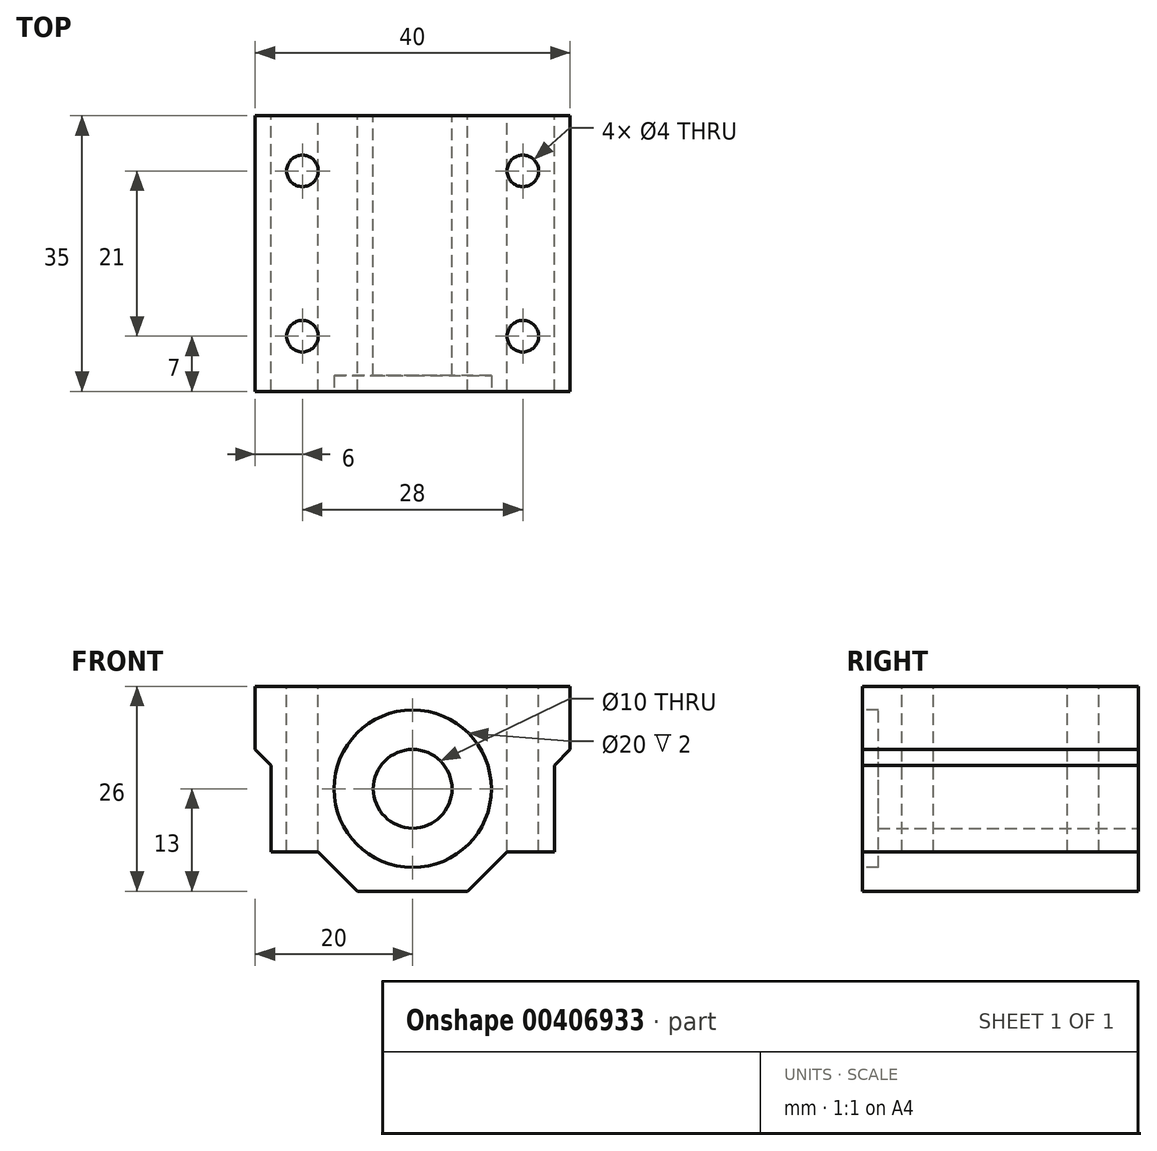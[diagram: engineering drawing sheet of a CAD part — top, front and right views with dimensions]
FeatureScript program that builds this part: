
annotation { "Feature Type Name" : "Feature", "Feature Type Description" : "" }
export const myFeature = defineFeature(function(context is Context, id is Id, definition is map)
    precondition{}
    {
        {
            var Q0;
            Q0=qCreatedBy(makeId("Front.planeOp"),FACE);
            var sketch = newSketch(context, id + "F0", { "sketchPlane" : qUnion([Q0])});
            skCircle(sketch, "E0", {"center": v(0, 0) * mm, "radius": 5 * mm});
            skLineSegment(sketch, "E1", {"start": v(-42.65, 13) * mm, "end": v(49.52, 13) * mm, "construction": true});
            skLineSegment(sketch, "E2", {"start": v(0, 13) * mm, "end": v(-20, 13) * mm});
            skLineSegment(sketch, "E3", {"start": v(-20, 13) * mm, "end": v(-20, 5) * mm});
            skLineSegment(sketch, "E4", {"start": v(-20, 5) * mm, "end": v(-18, 3) * mm});
            skLineSegment(sketch, "E5", {"start": v(-18, 3) * mm, "end": v(-18, -8) * mm});
            skLineSegment(sketch, "E6", {"start": v(-18, -8) * mm, "end": v(-12, -8) * mm});
            skLineSegment(sketch, "E7", {"start": v(-12, -8) * mm, "end": v(-7, -13) * mm});
            skLineSegment(sketch, "E8", {"start": v(-7, -13) * mm, "end": v(0, -13) * mm});
            skCircle(sketch, "E9", {"center": v(0, 0) * mm, "radius": 10 * mm, "construction": true});
            skLineSegment(sketch, "E10.MirrorCS", {"start": v(20, 13) * mm, "end": v(20, 5) * mm});
            skLineSegment(sketch, "E11.MirrorCS", {"start": v(20, 5) * mm, "end": v(18, 3) * mm});
            skLineSegment(sketch, "E12.MirrorCS", {"start": v(18, 3) * mm, "end": v(18, -8) * mm});
            skLineSegment(sketch, "E13.MirrorCS", {"start": v(18, -8) * mm, "end": v(12, -8) * mm});
            skLineSegment(sketch, "E14.MirrorCS", {"start": v(12, -8) * mm, "end": v(7, -13) * mm});
            skLineSegment(sketch, "E15.MirrorCS", {"start": v(7, -13) * mm, "end": v(0, -13) * mm});
            skLineSegment(sketch, "E16.MirrorCS", {"start": v(42.65, 13) * mm, "end": v(-49.52, 13) * mm, "construction": true});
            skLineSegment(sketch, "E17", {"start": v(0, 13) * mm, "end": v(20, 13) * mm});
            skSolve(sketch);
        }
        {
            var Q0;
            Q0 = qSketchRegion(id + "F0", true);
            extrude(context, id + "F1", {"entities" : qUnion([Q0]), "endBound" : BoundingType.SYMMETRIC, "depth" : 35 * mm});
        }
        {
            var Q0;
            Q0=makeQuery(id+"F1.opExtrude","CAP_FACE",FACE,{"disambiguationData":[OSD([sQuery(id+"F0.wireOp",EDGE,"E0"),sQuery(id+"F0.wireOp",EDGE,"E2"),sQuery(id+"F0.wireOp",EDGE,"E3"),sQuery(id+"F0.wireOp",EDGE,"E4"),sQuery(id+"F0.wireOp",EDGE,"E5"),sQuery(id+"F0.wireOp",EDGE,"E6"),sQuery(id+"F0.wireOp",EDGE,"E7"),sQuery(id+"F0.wireOp",EDGE,"E8"),sQuery(id+"F0.wireOp",EDGE,"E10.MirrorCS"),sQuery(id+"F0.wireOp",EDGE,"E11.MirrorCS"),sQuery(id+"F0.wireOp",EDGE,"E12.MirrorCS"),sQuery(id+"F0.wireOp",EDGE,"E13.MirrorCS"),sQuery(id+"F0.wireOp",EDGE,"E14.MirrorCS"),sQuery(id+"F0.wireOp",EDGE,"E15.MirrorCS"),sQuery(id+"F0.wireOp",EDGE,"E17")])],"isStart":false});
            var sketch = newSketch(context, id + "F2", { "sketchPlane" : qUnion([Q0])});
            skCircle(sketch, "E18", {"center": v(0, 0) * mm, "radius": 10 * mm});
            skSolve(sketch);
        }
        {
            var Q0;
            Q0 = qSketchRegion(id + "F2", true);
            extrude(context, id + "F3", {"entities" : qUnion([Q0]), "operationType" : NewBodyOperationType.REMOVE, "oppositeDirection" : true, "depth" : 2 * mm});
        }
        {
            var Q0;
            Q0=makeQuery(id+"F1.opExtrude","SWEPT_FACE",FACE,{"disambiguationData":[OSD([sQuery(id+"F0.wireOp",EDGE,"E2"),sQuery(id+"F0.wireOp",EDGE,"E17")])]});
            var sketch = newSketch(context, id + "F4", { "sketchPlane" : qUnion([Q0])});
            skLineSegment(sketch, "E19", {"start": v(-14, -17.5) * mm, "end": v(-14, 17.5) * mm, "construction": true});
            skCircle(sketch, "E20", {"center": v(-14, 10.5) * mm, "radius": 2 * mm});
            skCircle(sketch, "E21.MirrorC", {"center": v(-14, -10.5) * mm, "radius": 2 * mm});
            skCircle(sketch, "E22.MirrorC", {"center": v(14, 10.5) * mm, "radius": 2 * mm});
            skCircle(sketch, "E23.MirrorC", {"center": v(14, -10.5) * mm, "radius": 2 * mm});
            skSolve(sketch);
        }
        {
            var Q0;
            Q0 = qSketchRegion(id + "F4", true);
            extrude(context, id + "F5", {"entities" : qUnion([Q0]), "operationType" : NewBodyOperationType.REMOVE, "oppositeDirection" : true, "depth" : 25 * mm});
        }
    });
